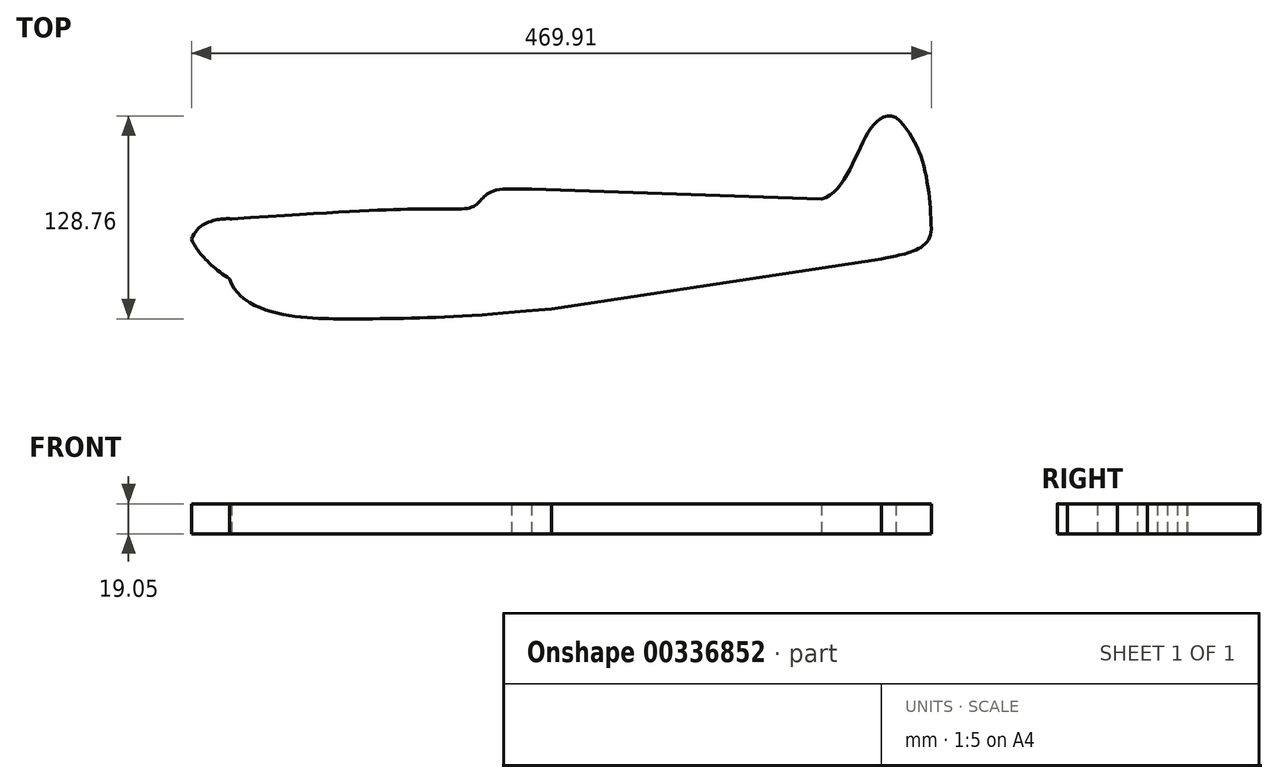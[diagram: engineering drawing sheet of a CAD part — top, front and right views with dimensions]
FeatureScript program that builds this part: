
annotation { "Feature Type Name" : "Feature", "Feature Type Description" : "" }
export const myFeature = defineFeature(function(context is Context, id is Id, definition is map)
    precondition{}
    {
        {
            var Q0;
            Q0=qCreatedBy(makeId("Top.planeOp"),FACE);
            var sketch = newSketch(context, id + "F0", { "sketchPlane" : qUnion([Q0])});
            skPoint(sketch, "E0.middle", {"position": v(0, 0) * mm});
            skLineSegment(sketch, "E1", {"start": v(-34.92, 12.7) * mm, "end": v(-22.22, 12.7) * mm});
            skLineSegment(sketch, "E2", {"start": v(161.93, 6.35) * mm, "end": v(-22.22, 12.7) * mm});
            skLineSegment(sketch, "E3", {"start": v(-9.53, -63.5) * mm, "end": v(200.03, -31.75) * mm});
            skFitSpline(sketch, "E4", {"points": [v(-212.72, -6.35) * mm, v(-238.13, -19.05) * mm], "startDerivative": vector(-12.32, 1.02) * mm, "endDerivative": vector(-15.3, -39.12) * mm});
            skFitSpline(sketch, "E5", {"points": [v(-212.72, -6.35) * mm, v(-66.67, 0) * mm], "startDerivative": vector(290.46, 19.05) * mm, "endDerivative": vector(110.39, 0) * mm});
            skFitSpline(sketch, "E6", {"points": [v(-238.13, -19.05) * mm, v(-213.75, -44.44) * mm], "startDerivative": vector(8.36, -21.61) * mm, "endDerivative": vector(38.34, -23.36) * mm});
            skPoint(sketch, "E7", {"position": v(-226.53, -31.75) * mm});
            skFitSpline(sketch, "E8", {"points": [v(-213.75, -44.44) * mm, v(-142.88, -69.85) * mm], "startDerivative": vector(23.14, -76.22) * mm, "endDerivative": vector(52.05, 0) * mm});
            skFitSpline(sketch, "E9", {"points": [v(-142.88, -69.85) * mm, v(-9.53, -63.5) * mm], "startDerivative": vector(117.56, 0) * mm, "endDerivative": vector(192.18, 19.05) * mm});
            skFitSpline(sketch, "E10", {"points": [v(209.39, 58.12) * mm, v(161.93, 6.35) * mm], "startDerivative": vector(-67.49, 23.86) * mm, "endDerivative": vector(-69, -15.88) * mm});
            skFitSpline(sketch, "E11", {"points": [v(231.78, -12.7) * mm, v(200.03, -31.75) * mm], "startDerivative": vector(-1.13, -47.5) * mm, "endDerivative": vector(-29.13, -7.54) * mm});
            skFitSpline(sketch, "E12", {"points": [v(-66.67, 0) * mm, v(-34.92, 12.7) * mm], "startDerivative": vector(48.85, 0) * mm, "endDerivative": vector(70.1, -1.4) * mm});
            skFitSpline(sketch, "E13", {"points": [v(209.39, 58.12) * mm, v(231.78, -12.7) * mm], "startDerivative": vector(57.03, -51.52) * mm, "endDerivative": vector(2.3, -73.3) * mm});
            skSolve(sketch);
        }
        {
            var Q0;
            Q0=makeQuery(id+"F0.imprint","IMPRINT",FACE,{"disambiguationData":[TD([[makeQuery(id+"F0.imprint","IMPRINT",EDGE,{"derivedFrom":sQuery(id+"F0.wireOp",EDGE,"E1")}),-1.0]])]});
            extrude(context, id + "F1", {"entities" : qUnion([Q0]), "depth" : 19.05 * mm});
        }
    });
